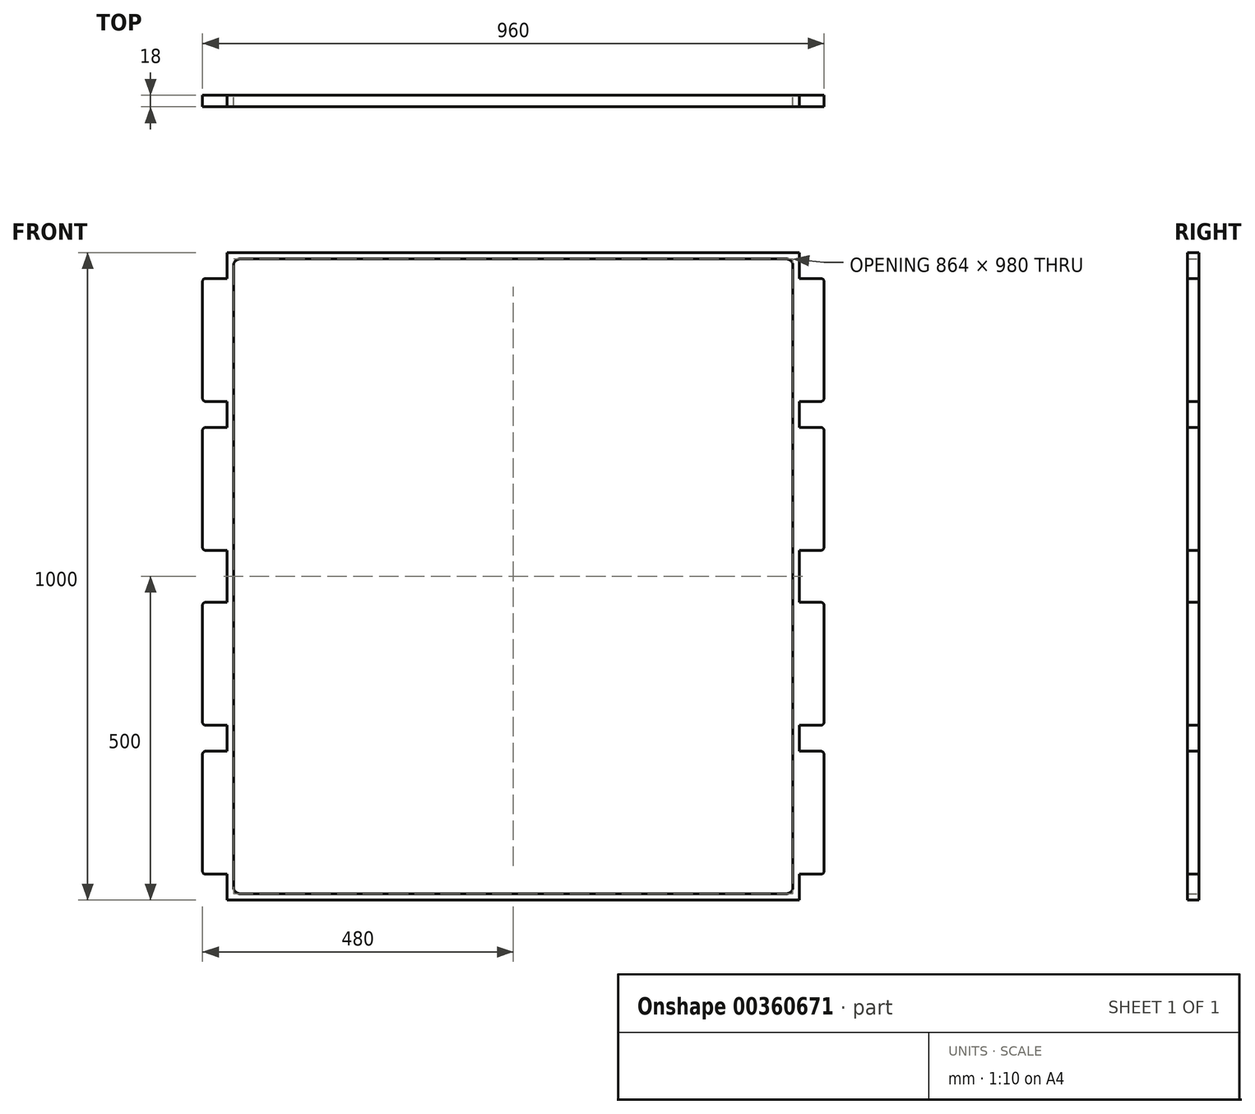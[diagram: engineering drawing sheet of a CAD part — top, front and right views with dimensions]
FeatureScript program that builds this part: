
annotation { "Feature Type Name" : "Feature", "Feature Type Description" : "" }
export const myFeature = defineFeature(function(context is Context, id is Id, definition is map)
    precondition{}
    {
        {
            var Q0;
            Q0=qCreatedBy(makeId("Front.planeOp"),FACE);
            var sketch = newSketch(context, id + "F0", { "sketchPlane" : qUnion([Q0])});
            skLineSegment(sketch, "E0.bottom", {"start": v(0, 0) * mm, "end": v(884, 0) * mm});
            skLineSegment(sketch, "E0.top", {"start": v(0, 1000) * mm, "end": v(884, 1000) * mm});
            skLineSegment(sketch, "E0.left", {"start": v(0, 0) * mm, "end": v(0, 40) * mm});
            skLineSegment(sketch, "E0.right", {"start": v(884, 0) * mm, "end": v(884, 40) * mm});
            skLineSegment(sketch, "E1.bottom", {"start": v(-33, 960) * mm, "end": v(0, 960) * mm});
            skLineSegment(sketch, "E1.top", {"start": v(-33, 770) * mm, "end": v(0, 770) * mm});
            skLineSegment(sketch, "E1.left", {"start": v(-38, 955) * mm, "end": v(-38, 775) * mm});
            skLineSegment(sketch, "E2.bottom", {"start": v(-33, 730) * mm, "end": v(0, 730) * mm});
            skLineSegment(sketch, "E2.top", {"start": v(-33, 540) * mm, "end": v(0, 540) * mm});
            skLineSegment(sketch, "E2.left", {"start": v(-38, 725) * mm, "end": v(-38, 545) * mm});
            skLineSegment(sketch, "E3.bottom", {"start": v(-33, 460) * mm, "end": v(0, 460) * mm});
            skLineSegment(sketch, "E3.top", {"start": v(-33, 270) * mm, "end": v(0, 270) * mm});
            skLineSegment(sketch, "E3.left", {"start": v(-38, 455) * mm, "end": v(-38, 275) * mm});
            skLineSegment(sketch, "E4.bottom", {"start": v(-33, 230) * mm, "end": v(0, 230) * mm});
            skLineSegment(sketch, "E4.top", {"start": v(-33, 40) * mm, "end": v(0, 40) * mm});
            skLineSegment(sketch, "E4.left", {"start": v(-38, 225) * mm, "end": v(-38, 45) * mm});
            skLineSegment(sketch, "E5.bottom", {"start": v(884, 230) * mm, "end": v(917, 230) * mm});
            skLineSegment(sketch, "E5.top", {"start": v(884, 40) * mm, "end": v(917, 40) * mm});
            skLineSegment(sketch, "E5.right", {"start": v(922, 225) * mm, "end": v(922, 45) * mm});
            skLineSegment(sketch, "E6.bottom", {"start": v(884, 460) * mm, "end": v(917, 460) * mm});
            skLineSegment(sketch, "E6.top", {"start": v(884, 270) * mm, "end": v(917, 270) * mm});
            skLineSegment(sketch, "E6.right", {"start": v(922, 455) * mm, "end": v(922, 275) * mm});
            skLineSegment(sketch, "E7.bottom", {"start": v(884, 540) * mm, "end": v(917, 540) * mm});
            skLineSegment(sketch, "E7.top", {"start": v(884, 730) * mm, "end": v(917, 730) * mm});
            skLineSegment(sketch, "E7.right", {"start": v(922, 545) * mm, "end": v(922, 725) * mm});
            skLineSegment(sketch, "E8.bottom", {"start": v(884, 770) * mm, "end": v(917, 770) * mm});
            skLineSegment(sketch, "E8.top", {"start": v(884, 960) * mm, "end": v(917, 960) * mm});
            skLineSegment(sketch, "E8.right", {"start": v(922, 775) * mm, "end": v(922, 955) * mm});
            skLineSegment(sketch, "E9.trimOffspring", {"start": v(0, 960) * mm, "end": v(0, 1000) * mm});
            skLineSegment(sketch, "E10.trimOffspring", {"start": v(0, 730) * mm, "end": v(0, 770) * mm});
            skLineSegment(sketch, "E11.trimOffspring", {"start": v(0, 460) * mm, "end": v(0, 540) * mm});
            skLineSegment(sketch, "E12.trimOffspring", {"start": v(0, 230) * mm, "end": v(0, 270) * mm});
            skLineSegment(sketch, "E13.trimOffspring", {"start": v(884, 230) * mm, "end": v(884, 270) * mm});
            skLineSegment(sketch, "E14.trimOffspring", {"start": v(884, 460) * mm, "end": v(884, 540) * mm});
            skLineSegment(sketch, "E15.trimOffspring", {"start": v(884, 730) * mm, "end": v(884, 770) * mm});
            skLineSegment(sketch, "E16.trimOffspring", {"start": v(884, 960) * mm, "end": v(884, 1000) * mm});
            skLineSegment(sketch, "E17.bottom", {"start": v(20, 990) * mm, "end": v(864, 990) * mm});
            skLineSegment(sketch, "E17.top", {"start": v(20, 10) * mm, "end": v(864, 10) * mm});
            skLineSegment(sketch, "E17.left", {"start": v(10, 980) * mm, "end": v(10, 20) * mm});
            skLineSegment(sketch, "E17.right", {"start": v(874, 980) * mm, "end": v(874, 20) * mm});
            skPoint(sketch, "E18.visualSharp", {"position": v(10, 990) * mm});
            skArc(sketch, "E18.filletArc", {"start": v(20, 990) * mm, "mid": v(12.93, 987.07) * mm, "end": v(10, 980) * mm});
            skPoint(sketch, "E19.visualSharp", {"position": v(874, 990) * mm});
            skArc(sketch, "E19.filletArc", {"start": v(874, 980) * mm, "mid": v(871.07, 987.07) * mm, "end": v(864, 990) * mm});
            skPoint(sketch, "E20.visualSharp", {"position": v(874, 10) * mm});
            skArc(sketch, "E20.filletArc", {"start": v(864, 10) * mm, "mid": v(871.07, 12.93) * mm, "end": v(874, 20) * mm});
            skPoint(sketch, "E21.visualSharp", {"position": v(10, 10) * mm});
            skArc(sketch, "E21.filletArc", {"start": v(10, 20) * mm, "mid": v(12.93, 12.93) * mm, "end": v(20, 10) * mm});
            skPoint(sketch, "E22.visualSharp", {"position": v(-38, 960) * mm});
            skArc(sketch, "E22.filletArc", {"start": v(-33, 960) * mm, "mid": v(-36.54, 958.54) * mm, "end": v(-38, 955) * mm});
            skPoint(sketch, "E23.visualSharp", {"position": v(-38, 770) * mm});
            skArc(sketch, "E23.filletArc", {"start": v(-38, 775) * mm, "mid": v(-36.54, 771.46) * mm, "end": v(-33, 770) * mm});
            skPoint(sketch, "E24.visualSharp", {"position": v(-38, 730) * mm});
            skArc(sketch, "E24.filletArc", {"start": v(-33, 730) * mm, "mid": v(-36.54, 728.54) * mm, "end": v(-38, 725) * mm});
            skPoint(sketch, "E25.visualSharp", {"position": v(-38, 540) * mm});
            skArc(sketch, "E25.filletArc", {"start": v(-38, 545) * mm, "mid": v(-36.54, 541.46) * mm, "end": v(-33, 540) * mm});
            skPoint(sketch, "E26.visualSharp", {"position": v(-38, 460) * mm});
            skArc(sketch, "E26.filletArc", {"start": v(-33, 460) * mm, "mid": v(-36.54, 458.54) * mm, "end": v(-38, 455) * mm});
            skPoint(sketch, "E27.visualSharp", {"position": v(-38, 270) * mm});
            skArc(sketch, "E27.filletArc", {"start": v(-38, 275) * mm, "mid": v(-36.54, 271.46) * mm, "end": v(-33, 270) * mm});
            skPoint(sketch, "E28.visualSharp", {"position": v(-38, 230) * mm});
            skArc(sketch, "E28.filletArc", {"start": v(-33, 230) * mm, "mid": v(-36.54, 228.54) * mm, "end": v(-38, 225) * mm});
            skPoint(sketch, "E29.visualSharp", {"position": v(-38, 40) * mm});
            skArc(sketch, "E29.filletArc", {"start": v(-38, 45) * mm, "mid": v(-36.54, 41.46) * mm, "end": v(-33, 40) * mm});
            skPoint(sketch, "E30.visualSharp", {"position": v(922, 40) * mm});
            skArc(sketch, "E30.filletArc", {"start": v(917, 40) * mm, "mid": v(920.54, 41.46) * mm, "end": v(922, 45) * mm});
            skPoint(sketch, "E31.visualSharp", {"position": v(922, 230) * mm});
            skArc(sketch, "E31.filletArc", {"start": v(922, 225) * mm, "mid": v(920.54, 228.54) * mm, "end": v(917, 230) * mm});
            skPoint(sketch, "E32.visualSharp", {"position": v(922, 270) * mm});
            skArc(sketch, "E32.filletArc", {"start": v(917, 270) * mm, "mid": v(920.54, 271.46) * mm, "end": v(922, 275) * mm});
            skPoint(sketch, "E33.visualSharp", {"position": v(922, 460) * mm});
            skArc(sketch, "E33.filletArc", {"start": v(922, 455) * mm, "mid": v(920.54, 458.54) * mm, "end": v(917, 460) * mm});
            skPoint(sketch, "E34.visualSharp", {"position": v(922, 540) * mm});
            skArc(sketch, "E34.filletArc", {"start": v(917, 540) * mm, "mid": v(920.54, 541.46) * mm, "end": v(922, 545) * mm});
            skPoint(sketch, "E35.visualSharp", {"position": v(922, 730) * mm});
            skArc(sketch, "E35.filletArc", {"start": v(922, 725) * mm, "mid": v(920.54, 728.54) * mm, "end": v(917, 730) * mm});
            skPoint(sketch, "E36.visualSharp", {"position": v(922, 770) * mm});
            skArc(sketch, "E36.filletArc", {"start": v(917, 770) * mm, "mid": v(920.54, 771.46) * mm, "end": v(922, 775) * mm});
            skPoint(sketch, "E37.visualSharp", {"position": v(922, 960) * mm});
            skArc(sketch, "E37.filletArc", {"start": v(922, 955) * mm, "mid": v(920.54, 958.54) * mm, "end": v(917, 960) * mm});
            skSolve(sketch);
        }
        {
            var Q0;
            Q0=makeQuery(id+"F0.imprint","IMPRINT",FACE,{"disambiguationData":[TD([[makeQuery(id+"F0.imprint","IMPRINT",EDGE,{"derivedFrom":sQuery(id+"F0.wireOp",EDGE,"E0.bottom")}),1.0]])]});
            extrude(context, id + "F1", {"entities" : qUnion([Q0]), "depth" : 18 * mm});
        }
    });
